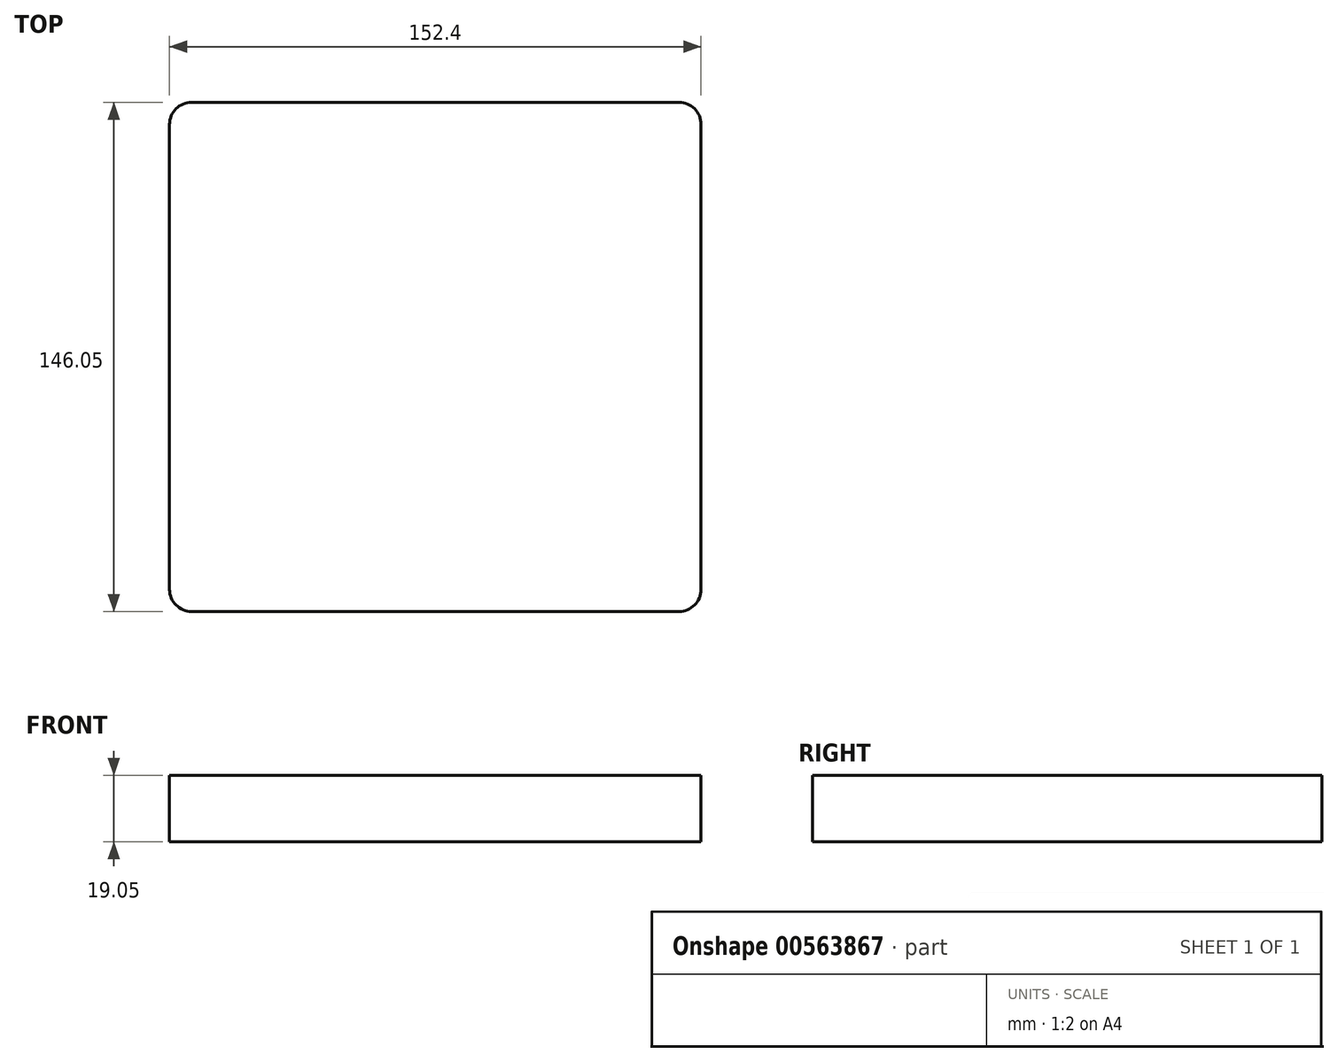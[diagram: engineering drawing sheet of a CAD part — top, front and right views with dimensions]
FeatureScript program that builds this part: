
annotation { "Feature Type Name" : "Feature", "Feature Type Description" : "" }
export const myFeature = defineFeature(function(context is Context, id is Id, definition is map)
    precondition{}
    {
        {
            var Q0;
            Q0=qCreatedBy(makeId("Top.planeOp"),FACE);
            var sketch = newSketch(context, id + "F0", { "sketchPlane" : qUnion([Q0])});
            skLineSegment(sketch, "E0.bottom", {"start": v(6.35, 0) * mm, "end": v(146.05, 0) * mm});
            skLineSegment(sketch, "E0.top", {"start": v(6.35, 146.05) * mm, "end": v(146.05, 146.05) * mm});
            skLineSegment(sketch, "E0.left", {"start": v(0, 6.35) * mm, "end": v(0, 139.7) * mm});
            skLineSegment(sketch, "E0.right", {"start": v(152.4, 6.35) * mm, "end": v(152.4, 139.7) * mm});
            skPoint(sketch, "E1.visualSharp", {"position": v(0, 0) * mm});
            skArc(sketch, "E1.filletArc", {"start": v(0, 6.35) * mm, "mid": v(1.86, 1.86) * mm, "end": v(6.35, 0) * mm});
            skPoint(sketch, "E2.visualSharp", {"position": v(152.4, 0) * mm});
            skArc(sketch, "E2.filletArc", {"start": v(146.05, 0) * mm, "mid": v(150.54, 1.86) * mm, "end": v(152.4, 6.35) * mm});
            skPoint(sketch, "E3.visualSharp", {"position": v(152.4, 146.05) * mm});
            skArc(sketch, "E3.filletArc", {"start": v(152.4, 139.7) * mm, "mid": v(150.54, 144.2) * mm, "end": v(146.05, 146.05) * mm});
            skPoint(sketch, "E4.visualSharp", {"position": v(0, 146.05) * mm});
            skArc(sketch, "E4.filletArc", {"start": v(6.35, 146.05) * mm, "mid": v(1.86, 144.2) * mm, "end": v(0, 139.7) * mm});
            skSolve(sketch);
        }
        {
            var Q0;
            Q0=makeQuery(id+"F0.imprint","IMPRINT",FACE,{"disambiguationData":[TD([[makeQuery(id+"F0.imprint","IMPRINT",EDGE,{"derivedFrom":sQuery(id+"F0.wireOp",EDGE,"E0.bottom")}),1.0]])]});
            extrude(context, id + "F1", {"entities" : qUnion([Q0]), "depth" : 19.05 * mm, "offsetDistance" : 25.4 * mm});
        }
    });
